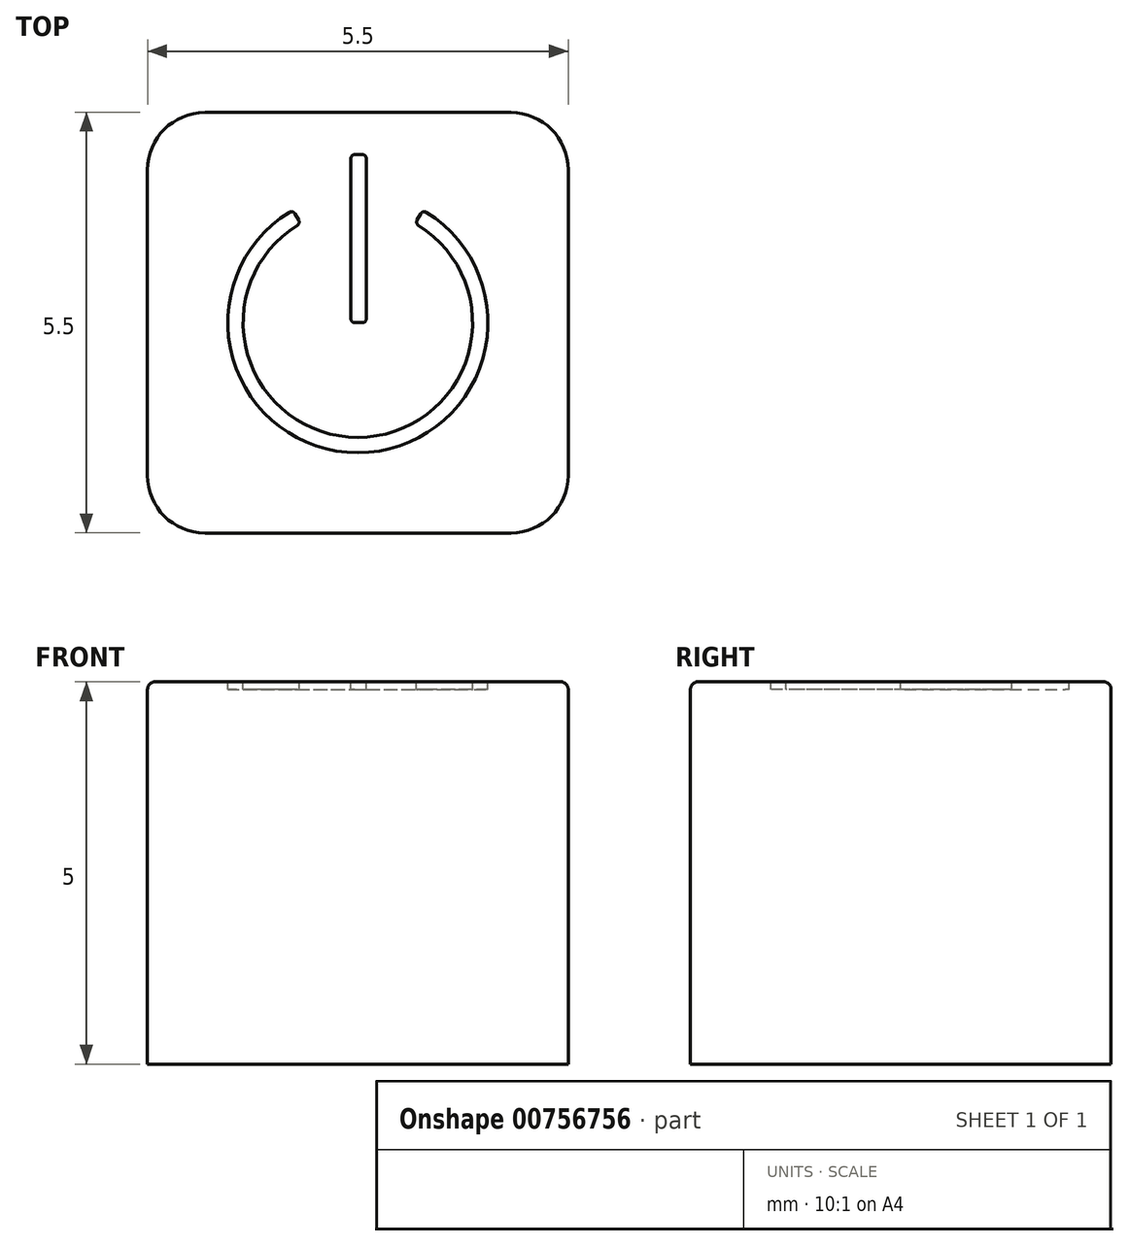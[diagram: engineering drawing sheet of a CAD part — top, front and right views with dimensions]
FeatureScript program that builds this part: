
annotation { "Feature Type Name" : "Feature", "Feature Type Description" : "" }
export const myFeature = defineFeature(function(context is Context, id is Id, definition is map)
    precondition{}
    {
        {
            var Q0;
            Q0=qCreatedBy(makeId("Top.planeOp"),FACE);
            var sketch = newSketch(context, id + "F0", { "sketchPlane" : qUnion([Q0])});
            skLineSegment(sketch, "E0.bottom", {"start": v(16.68, 58.74) * mm, "end": v(20.68, 58.74) * mm, "construction": true});
            skLineSegment(sketch, "E0.top", {"start": v(16.68, 52.74) * mm, "end": v(20.68, 52.74) * mm, "construction": true});
            skLineSegment(sketch, "E0.left", {"start": v(15.68, 57.74) * mm, "end": v(15.68, 53.74) * mm, "construction": true});
            skLineSegment(sketch, "E0.right", {"start": v(21.68, 57.74) * mm, "end": v(21.68, 53.74) * mm, "construction": true});
            skPoint(sketch, "E1.visualSharp", {"position": v(15.68, 58.74) * mm});
            skArc(sketch, "E1.filletArc", {"start": v(16.68, 58.74) * mm, "mid": v(15.97, 58.44) * mm, "end": v(15.68, 57.74) * mm, "construction": true});
            skPoint(sketch, "E2.visualSharp", {"position": v(15.68, 52.74) * mm});
            skArc(sketch, "E2.filletArc", {"start": v(15.68, 53.74) * mm, "mid": v(15.97, 53.03) * mm, "end": v(16.68, 52.74) * mm, "construction": true});
            skPoint(sketch, "E3.visualSharp", {"position": v(21.68, 52.74) * mm});
            skArc(sketch, "E3.filletArc", {"start": v(20.68, 52.74) * mm, "mid": v(21.39, 53.03) * mm, "end": v(21.68, 53.74) * mm, "construction": true});
            skPoint(sketch, "E4.visualSharp", {"position": v(21.68, 58.74) * mm});
            skArc(sketch, "E4.filletArc", {"start": v(21.68, 57.74) * mm, "mid": v(21.39, 58.44) * mm, "end": v(20.68, 58.74) * mm, "construction": true});
            skArc(sketch, "E5.0", {"start": v(16.68, 58.49) * mm, "mid": v(16.15, 58.27) * mm, "end": v(15.93, 57.74) * mm});
            skLineSegment(sketch, "E5.1", {"start": v(15.93, 57.74) * mm, "end": v(15.93, 53.74) * mm});
            skLineSegment(sketch, "E5.2", {"start": v(16.68, 58.49) * mm, "end": v(20.68, 58.49) * mm});
            skArc(sketch, "E5.3", {"start": v(15.93, 53.74) * mm, "mid": v(16.15, 53.2) * mm, "end": v(16.68, 52.99) * mm});
            skArc(sketch, "E5.4", {"start": v(21.43, 57.74) * mm, "mid": v(21.2, 58.27) * mm, "end": v(20.68, 58.49) * mm});
            skLineSegment(sketch, "E5.5", {"start": v(21.43, 57.74) * mm, "end": v(21.43, 53.74) * mm});
            skArc(sketch, "E5.6", {"start": v(20.68, 52.99) * mm, "mid": v(21.2, 53.2) * mm, "end": v(21.43, 53.74) * mm});
            skLineSegment(sketch, "E5.7", {"start": v(16.68, 52.99) * mm, "end": v(20.68, 52.99) * mm});
            skSolve(sketch);
        }
        {
            var Q0;
            Q0=makeQuery(id+"F0.imprint","IMPRINT",FACE,{"disambiguationData":[TD([[makeQuery(id+"F0.imprint","IMPRINT",EDGE,{"derivedFrom":sQuery(id+"F0.wireOp",EDGE,"E5.0")}),1.0]])]});
            extrude(context, id + "F1", {"entities" : qUnion([Q0]), "depth" : 5 * mm, "offsetDistance" : 25 * mm});
        }
        {
            var Q0;
            Q0=makeQuery(id+"F1.opExtrude","CAP_FACE",FACE,{"disambiguationData":[OSD([sQuery(id+"F0.wireOp",EDGE,"E5.0"),sQuery(id+"F0.wireOp",EDGE,"E5.1"),sQuery(id+"F0.wireOp",EDGE,"E5.2"),sQuery(id+"F0.wireOp",EDGE,"E5.3"),sQuery(id+"F0.wireOp",EDGE,"E5.4"),sQuery(id+"F0.wireOp",EDGE,"E5.5"),sQuery(id+"F0.wireOp",EDGE,"E5.6"),sQuery(id+"F0.wireOp",EDGE,"E5.7")])],"isStart":false});
            var sketch = newSketch(context, id + "F2", { "sketchPlane" : qUnion([Q0])});
            skLineSegment(sketch, "E6", {"start": v(18.68, 58.49) * mm, "end": v(18.68, 52.99) * mm, "construction": true});
            skLineSegment(sketch, "E7", {"start": v(18.64, 55.74) * mm, "end": v(18.74, 55.74) * mm, "construction": true});
            skLineSegment(sketch, "E8", {"start": v(19.45, 57.08) * mm, "end": v(20.15, 58.29) * mm, "construction": true});
            skArc(sketch, "E9", {"start": v(19.47, 57.01) * mm, "mid": v(20.12, 55.33) * mm, "end": v(18.68, 54.24) * mm});
            skArc(sketch, "E10.MirrorCS", {"start": v(17.89, 57.01) * mm, "mid": v(17.24, 55.33) * mm, "end": v(18.68, 54.24) * mm});
            skArc(sketch, "E11.0", {"start": v(17.78, 57.18) * mm, "mid": v(17.04, 55.27) * mm, "end": v(18.68, 54.04) * mm});
            skArc(sketch, "E11.1", {"start": v(19.57, 57.18) * mm, "mid": v(20.31, 55.27) * mm, "end": v(18.68, 54.04) * mm});
            skLineSegment(sketch, "E12", {"start": v(17.85, 57.17) * mm, "end": v(17.9, 57.08) * mm});
            skLineSegment(sketch, "E13", {"start": v(19.5, 57.17) * mm, "end": v(19.43, 57.04) * mm});
            skLineSegment(sketch, "E14.bottom", {"start": v(18.59, 55.74) * mm, "end": v(18.79, 55.74) * mm});
            skLineSegment(sketch, "E14.top", {"start": v(18.64, 57.94) * mm, "end": v(18.74, 57.94) * mm});
            skLineSegment(sketch, "E14.left", {"start": v(18.59, 55.79) * mm, "end": v(18.59, 57.89) * mm});
            skLineSegment(sketch, "E14.right", {"start": v(18.79, 55.79) * mm, "end": v(18.79, 57.89) * mm});
            skPoint(sketch, "E15.visualSharp", {"position": v(18.59, 57.94) * mm});
            skArc(sketch, "E15.filletArc", {"start": v(18.64, 57.94) * mm, "mid": v(18.6, 57.92) * mm, "end": v(18.59, 57.89) * mm});
            skPoint(sketch, "E16.visualSharp", {"position": v(18.79, 57.94) * mm});
            skArc(sketch, "E16.filletArc", {"start": v(18.79, 57.89) * mm, "mid": v(18.77, 57.92) * mm, "end": v(18.74, 57.94) * mm});
            skPoint(sketch, "E17.newPointB", {"position": v(15.93, 55.74) * mm});
            skArc(sketch, "E17.filletArc", {"start": v(18.59, 55.79) * mm, "mid": v(18.6, 55.75) * mm, "end": v(18.64, 55.74) * mm});
            skPoint(sketch, "E18.newPointA", {"position": v(21.43, 55.74) * mm});
            skPoint(sketch, "E18.newPointB", {"position": v(18.79, 55.74) * mm});
            skArc(sketch, "E18.filletArc", {"start": v(18.74, 55.74) * mm, "mid": v(18.77, 55.75) * mm, "end": v(18.79, 55.79) * mm});
            skPoint(sketch, "E19.visualSharp", {"position": v(17.83, 57.2) * mm});
            skArc(sketch, "E19.filletArc", {"start": v(17.85, 57.17) * mm, "mid": v(17.82, 57.19) * mm, "end": v(17.78, 57.18) * mm});
            skPoint(sketch, "E20.visualSharp", {"position": v(17.93, 57.04) * mm});
            skArc(sketch, "E20.filletArc", {"start": v(17.89, 57.01) * mm, "mid": v(17.9, 57.04) * mm, "end": v(17.9, 57.08) * mm});
            skPoint(sketch, "E21.visualSharp", {"position": v(19.53, 57.2) * mm});
            skArc(sketch, "E21.filletArc", {"start": v(19.57, 57.18) * mm, "mid": v(19.53, 57.19) * mm, "end": v(19.5, 57.17) * mm});
            skPoint(sketch, "E22.newPointB", {"position": v(19.43, 57.04) * mm});
            skArc(sketch, "E22.filletArc", {"start": v(19.45, 57.08) * mm, "mid": v(19.45, 57.04) * mm, "end": v(19.47, 57.01) * mm});
            skSolve(sketch);
        }
        {
            var Q0;
            Q0 = qSketchRegion(id + "F2", true);
            extrude(context, id + "F3", {"entities" : qUnion([Q0]), "operationType" : NewBodyOperationType.REMOVE, "oppositeDirection" : true, "depth" : 0.1 * mm, "offsetDistance" : 25 * mm});
        }
        {
            var Q0;
            Q0=makeQuery(id+"F1.opExtrude","CAP_EDGE",EDGE,{"disambiguationData":[OSD([sQuery(id+"F0.wireOp",EDGE,"E5.2")])],"isStart":false});
            var Q1;
            Q1=makeQuery(id+"F1.opExtrude","CAP_EDGE",EDGE,{"disambiguationData":[OSD([sQuery(id+"F0.wireOp",EDGE,"E5.0")])],"isStart":false});
            var Q2;
            Q2=makeQuery(id+"F1.opExtrude","CAP_EDGE",EDGE,{"disambiguationData":[OSD([sQuery(id+"F0.wireOp",EDGE,"E5.1")])],"isStart":false});
            var Q3;
            Q3=makeQuery(id+"F1.opExtrude","CAP_EDGE",EDGE,{"disambiguationData":[OSD([sQuery(id+"F0.wireOp",EDGE,"E5.3")])],"isStart":false});
            var Q4;
            Q4=makeQuery(id+"F1.opExtrude","CAP_EDGE",EDGE,{"disambiguationData":[OSD([sQuery(id+"F0.wireOp",EDGE,"E5.6")])],"isStart":false});
            var Q5;
            Q5=makeQuery(id+"F1.opExtrude","CAP_EDGE",EDGE,{"disambiguationData":[OSD([sQuery(id+"F0.wireOp",EDGE,"E5.7")])],"isStart":false});
            var Q6;
            Q6=makeQuery(id+"F1.opExtrude","CAP_EDGE",EDGE,{"disambiguationData":[OSD([sQuery(id+"F0.wireOp",EDGE,"E5.5")])],"isStart":false});
            var Q7;
            Q7=makeQuery(id+"F1.opExtrude","CAP_EDGE",EDGE,{"disambiguationData":[OSD([sQuery(id+"F0.wireOp",EDGE,"E5.4")])],"isStart":false});
            fillet(context, id + "F4", {"entities" : qUnion([Q0, Q1, Q2, Q3, Q4, Q5, Q6, Q7]), "radius" : 0.1 * mm, "tangentPropagation" : true, "allowEdgeOverflow" : false});
        }
    });
